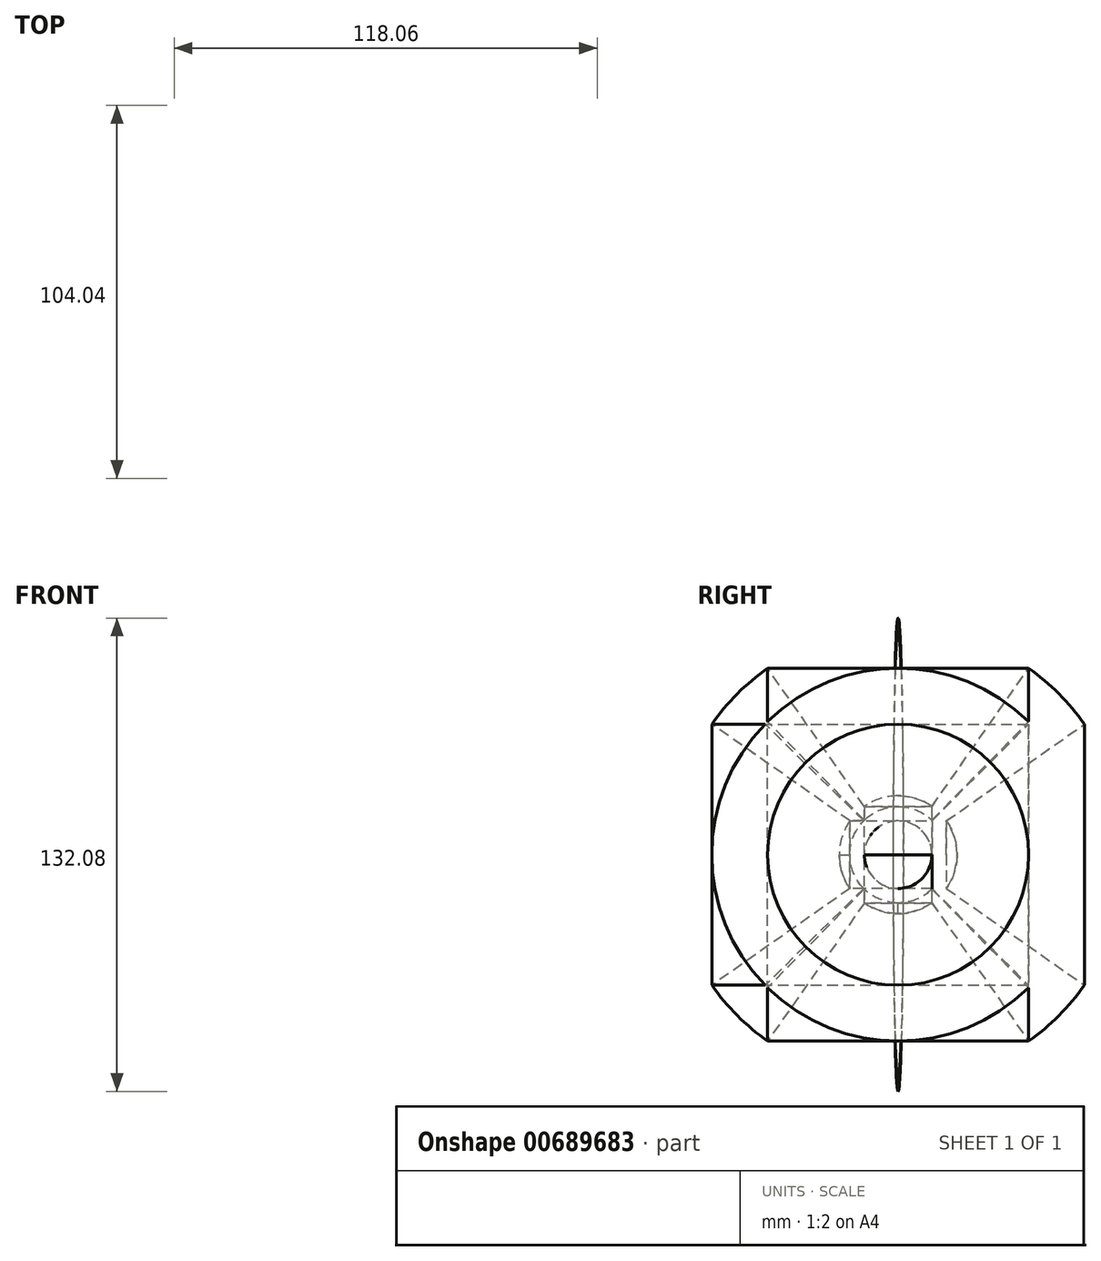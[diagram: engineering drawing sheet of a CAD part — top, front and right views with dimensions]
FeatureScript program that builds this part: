
annotation { "Feature Type Name" : "Feature", "Feature Type Description" : "" }
export const myFeature = defineFeature(function(context is Context, id is Id, definition is map)
    precondition{}
    {
        {
            var Q0;
            Q0=qCreatedBy(makeId("Front.planeOp"),FACE);
            var sketch = newSketch(context, id + "F0", { "sketchPlane" : qUnion([Q0])});
            skLineSegment(sketch, "E0", {"start": v(0, 0) * mm, "end": v(0, 63.5) * mm});
            skLineSegment(sketch, "E1", {"start": v(0, 0) * mm, "end": v(63.5, 0) * mm});
            skArc(sketch, "E2", {"start": v(63.5, 0) * mm, "mid": v(44.9, 44.9) * mm, "end": v(0, 63.5) * mm});
            skPoint(sketch, "E3", {"position": v(0, 16.43) * mm});
            skPoint(sketch, "E4", {"position": v(0, 31.75) * mm});
            skPoint(sketch, "E5", {"position": v(0, 44.9) * mm});
            skPoint(sketch, "E6", {"position": v(0, 55) * mm});
            skPoint(sketch, "E7", {"position": v(0, 61.33) * mm});
            skLineSegment(sketch, "E8", {"start": v(0, 16.43) * mm, "end": v(61.34, 16.43) * mm});
            skLineSegment(sketch, "E9", {"start": v(0, 31.75) * mm, "end": v(55, 31.75) * mm});
            skLineSegment(sketch, "E10", {"start": v(0, 44.9) * mm, "end": v(44.9, 44.9) * mm});
            skLineSegment(sketch, "E11", {"start": v(0, 55) * mm, "end": v(31.75, 55) * mm});
            skLineSegment(sketch, "E12", {"start": v(0, 61.33) * mm, "end": v(16.44, 61.33) * mm});
            skLineSegment(sketch, "E13", {"start": v(61.34, 16.43) * mm, "end": v(61.34, 0) * mm});
            skLineSegment(sketch, "E14", {"start": v(16.44, 61.33) * mm, "end": v(16.44, 0) * mm});
            skLineSegment(sketch, "E15", {"start": v(31.75, 55) * mm, "end": v(31.75, 0) * mm});
            skLineSegment(sketch, "E16", {"start": v(44.9, 44.9) * mm, "end": v(44.9, 0) * mm});
            skLineSegment(sketch, "E17", {"start": v(55, 31.75) * mm, "end": v(55, 0) * mm});
            skSolve(sketch);
        }
        {
            var Q0;
            {var subQ0=sQuery(id+"F0.wireOp",EDGE,"E1");var subQ1=sQuery(id+"F0.wireOp",EDGE,"E0");var subQ2=makeQuery(id+"F0.imprint","INTERSECT",VERTEX,{"derivedFrom":[subQ1,subQ0]});Q0=makeQuery(id+"F0.imprint","IMPRINT",FACE,{"disambiguationData":[TD([[makeQuery(id+"F0.imprint","IMPRINT",EDGE,{"disambiguationData":[TD([[subQ2,-1.0]])],"derivedFrom":subQ1}),-1.0]])]});}
            var Q1;
            {var subQ0=sQuery(id+"F0.wireOp",EDGE,"E15");var subQ1=sQuery(id+"F0.wireOp",EDGE,"E8");var subQ2=makeQuery(id+"F0.imprint","INTERSECT",VERTEX,{"derivedFrom":[subQ1,subQ0]});Q1=makeQuery(id+"F0.imprint","IMPRINT",FACE,{"disambiguationData":[TD([[makeQuery(id+"F0.imprint","IMPRINT",EDGE,{"disambiguationData":[TD([[subQ2,-1.0]])],"derivedFrom":subQ1}),1.0]])]});}
            var Q2;
            {var subQ0=sQuery(id+"F0.wireOp",EDGE,"E13");Q2=makeQuery(id+"F0.imprint","IMPRINT",FACE,{"disambiguationData":[TD([[makeQuery(id+"F0.imprint","IMPRINT",EDGE,{"derivedFrom":subQ0}),-1.0]])]});}
            var Q3;
            {var subQ3=sQuery(id+"F0.wireOp",EDGE,"E13");Q3=makeQuery(id+"F0.imprint","IMPRINT",FACE,{"disambiguationData":[TD([[makeQuery(id+"F0.imprint","IMPRINT",EDGE,{"derivedFrom":subQ3}),1.0]])]});}
            var Q4;
            {var subQ0=sQuery(id+"F0.wireOp",EDGE,"E14");var subQ1=sQuery(id+"F0.wireOp",EDGE,"E10");var subQ2=makeQuery(id+"F0.imprint","INTERSECT",VERTEX,{"derivedFrom":[subQ1,subQ0]});Q4=makeQuery(id+"F0.imprint","IMPRINT",FACE,{"disambiguationData":[TD([[makeQuery(id+"F0.imprint","IMPRINT",EDGE,{"disambiguationData":[TD([[subQ2,-1.0]])],"derivedFrom":subQ1}),1.0]])]});}
            var Q5;
            {var subQ3=sQuery(id+"F0.wireOp",EDGE,"E12");Q5=makeQuery(id+"F0.imprint","IMPRINT",FACE,{"disambiguationData":[TD([[makeQuery(id+"F0.imprint","IMPRINT",EDGE,{"derivedFrom":subQ3}),1.0]])]});}
            var Q6;
            {var subQ0=sQuery(id+"F0.wireOp",EDGE,"E16");var subQ1=sQuery(id+"F0.wireOp",EDGE,"E1");var subQ2=makeQuery(id+"F0.imprint","INTERSECT",VERTEX,{"derivedFrom":[subQ1,subQ0]});Q6=makeQuery(id+"F0.imprint","IMPRINT",FACE,{"disambiguationData":[TD([[makeQuery(id+"F0.imprint","IMPRINT",EDGE,{"disambiguationData":[TD([[subQ2,-1.0]])],"derivedFrom":subQ1}),1.0]])]});}
            var Q7;
            {var subQ0=sQuery(id+"F0.wireOp",EDGE,"E8");var subQ3=sQuery(id+"F0.wireOp",EDGE,"E17");var subQ5=makeQuery(id+"F0.imprint","INTERSECT",VERTEX,{"derivedFrom":[subQ0,subQ3]});Q7=makeQuery(id+"F0.imprint","IMPRINT",FACE,{"disambiguationData":[TD([[makeQuery(id+"F0.imprint","IMPRINT",EDGE,{"disambiguationData":[TD([[subQ5,-1.0]])],"derivedFrom":subQ0}),1.0]])]});}
            var Q8;
            {var subQ0=sQuery(id+"F0.wireOp",EDGE,"E9");var subQ3=sQuery(id+"F0.wireOp",EDGE,"E16");var subQ5=makeQuery(id+"F0.imprint","INTERSECT",VERTEX,{"derivedFrom":[subQ0,subQ3]});Q8=makeQuery(id+"F0.imprint","IMPRINT",FACE,{"disambiguationData":[TD([[makeQuery(id+"F0.imprint","IMPRINT",EDGE,{"disambiguationData":[TD([[subQ5,-1.0]])],"derivedFrom":subQ0}),1.0]])]});}
            var Q9;
            {var subQ0=sQuery(id+"F0.wireOp",EDGE,"E14");var subQ1=sQuery(id+"F0.wireOp",EDGE,"E9");var subQ2=makeQuery(id+"F0.imprint","INTERSECT",VERTEX,{"derivedFrom":[subQ1,subQ0]});Q9=makeQuery(id+"F0.imprint","IMPRINT",FACE,{"disambiguationData":[TD([[makeQuery(id+"F0.imprint","IMPRINT",EDGE,{"disambiguationData":[TD([[subQ2,-1.0]])],"derivedFrom":subQ1}),1.0]])]});}
            var Q10;
            {var subQ0=sQuery(id+"F0.wireOp",EDGE,"E14");var subQ1=sQuery(id+"F0.wireOp",EDGE,"E8");var subQ2=makeQuery(id+"F0.imprint","INTERSECT",VERTEX,{"derivedFrom":[subQ1,subQ0]});Q10=makeQuery(id+"F0.imprint","IMPRINT",FACE,{"disambiguationData":[TD([[makeQuery(id+"F0.imprint","IMPRINT",EDGE,{"disambiguationData":[TD([[subQ2,-1.0]])],"derivedFrom":subQ1}),1.0]])]});}
            var Q11;
            {var subQ0=sQuery(id+"F0.wireOp",EDGE,"E10");var subQ3=sQuery(id+"F0.wireOp",EDGE,"E15");var subQ5=makeQuery(id+"F0.imprint","INTERSECT",VERTEX,{"derivedFrom":[subQ0,subQ3]});Q11=makeQuery(id+"F0.imprint","IMPRINT",FACE,{"disambiguationData":[TD([[makeQuery(id+"F0.imprint","IMPRINT",EDGE,{"disambiguationData":[TD([[subQ5,-1.0]])],"derivedFrom":subQ0}),1.0]])]});}
            var Q12;
            {var subQ0=sQuery(id+"F0.wireOp",EDGE,"E11");var subQ3=sQuery(id+"F0.wireOp",EDGE,"E14");var subQ5=makeQuery(id+"F0.imprint","INTERSECT",VERTEX,{"derivedFrom":[subQ0,subQ3]});Q12=makeQuery(id+"F0.imprint","IMPRINT",FACE,{"disambiguationData":[TD([[makeQuery(id+"F0.imprint","IMPRINT",EDGE,{"disambiguationData":[TD([[subQ5,-1.0]])],"derivedFrom":subQ0}),1.0]])]});}
            var Q13;
            {var subQ0=sQuery(id+"F0.wireOp",EDGE,"E8");var subQ1=sQuery(id+"F0.wireOp",EDGE,"E0");var subQ2=makeQuery(id+"F0.imprint","INTERSECT",VERTEX,{"derivedFrom":[subQ1,subQ0]});Q13=makeQuery(id+"F0.imprint","IMPRINT",FACE,{"disambiguationData":[TD([[makeQuery(id+"F0.imprint","IMPRINT",EDGE,{"disambiguationData":[TD([[subQ2,-1.0]])],"derivedFrom":subQ1}),-1.0]])]});}
            var Q14;
            {var subQ0=sQuery(id+"F0.wireOp",EDGE,"E9");var subQ1=sQuery(id+"F0.wireOp",EDGE,"E0");var subQ2=makeQuery(id+"F0.imprint","INTERSECT",VERTEX,{"derivedFrom":[subQ1,subQ0]});Q14=makeQuery(id+"F0.imprint","IMPRINT",FACE,{"disambiguationData":[TD([[makeQuery(id+"F0.imprint","IMPRINT",EDGE,{"disambiguationData":[TD([[subQ2,-1.0]])],"derivedFrom":subQ1}),-1.0]])]});}
            var Q15;
            {var subQ0=sQuery(id+"F0.wireOp",EDGE,"E10");var subQ1=sQuery(id+"F0.wireOp",EDGE,"E0");var subQ2=makeQuery(id+"F0.imprint","INTERSECT",VERTEX,{"derivedFrom":[subQ1,subQ0]});Q15=makeQuery(id+"F0.imprint","IMPRINT",FACE,{"disambiguationData":[TD([[makeQuery(id+"F0.imprint","IMPRINT",EDGE,{"disambiguationData":[TD([[subQ2,-1.0]])],"derivedFrom":subQ1}),-1.0]])]});}
            var Q16;
            {var subQ3=sQuery(id+"F0.wireOp",EDGE,"E12");Q16=makeQuery(id+"F0.imprint","IMPRINT",FACE,{"disambiguationData":[TD([[makeQuery(id+"F0.imprint","IMPRINT",EDGE,{"derivedFrom":subQ3}),-1.0]])]});}
            var Q17;
            {var subQ0=sQuery(id+"F0.wireOp",EDGE,"E16");var subQ1=sQuery(id+"F0.wireOp",EDGE,"E8");var subQ2=makeQuery(id+"F0.imprint","INTERSECT",VERTEX,{"derivedFrom":[subQ1,subQ0]});Q17=makeQuery(id+"F0.imprint","IMPRINT",FACE,{"disambiguationData":[TD([[makeQuery(id+"F0.imprint","IMPRINT",EDGE,{"disambiguationData":[TD([[subQ2,-1.0]])],"derivedFrom":subQ1}),1.0]])]});}
            var Q18;
            {var subQ0=sQuery(id+"F0.wireOp",EDGE,"E15");var subQ1=sQuery(id+"F0.wireOp",EDGE,"E9");var subQ2=makeQuery(id+"F0.imprint","INTERSECT",VERTEX,{"derivedFrom":[subQ1,subQ0]});Q18=makeQuery(id+"F0.imprint","IMPRINT",FACE,{"disambiguationData":[TD([[makeQuery(id+"F0.imprint","IMPRINT",EDGE,{"disambiguationData":[TD([[subQ2,-1.0]])],"derivedFrom":subQ1}),1.0]])]});}
            var Q19;
            {var subQ0=sQuery(id+"F0.wireOp",EDGE,"E14");var subQ1=sQuery(id+"F0.wireOp",EDGE,"E1");var subQ2=makeQuery(id+"F0.imprint","INTERSECT",VERTEX,{"derivedFrom":[subQ1,subQ0]});Q19=makeQuery(id+"F0.imprint","IMPRINT",FACE,{"disambiguationData":[TD([[makeQuery(id+"F0.imprint","IMPRINT",EDGE,{"disambiguationData":[TD([[subQ2,-1.0]])],"derivedFrom":subQ1}),1.0]])]});}
            var Q20;
            {var subQ0=sQuery(id+"F0.wireOp",EDGE,"E15");var subQ1=sQuery(id+"F0.wireOp",EDGE,"E1");var subQ2=makeQuery(id+"F0.imprint","INTERSECT",VERTEX,{"derivedFrom":[subQ1,subQ0]});Q20=makeQuery(id+"F0.imprint","IMPRINT",FACE,{"disambiguationData":[TD([[makeQuery(id+"F0.imprint","IMPRINT",EDGE,{"disambiguationData":[TD([[subQ2,-1.0]])],"derivedFrom":subQ1}),1.0]])]});}
            var Q21;
            Q21=sQuery(id+"F0.wireOp",EDGE,"E14");
            var Q22;
            Q22=sQuery(id+"F0.wireOp",EDGE,"E15");
            var Q23;
            Q23=sQuery(id+"F0.wireOp",EDGE,"E16");
            var Q24;
            Q24=sQuery(id+"F0.wireOp",EDGE,"E17");
            var Q25;
            Q25=sQuery(id+"F0.wireOp",EDGE,"E13");
            var Q26;
            Q26=sQuery(id+"F0.wireOp",EDGE,"E0");
            revolve(context, id + "F1", {"bodyType" : ToolBodyType.SURFACE, "entities" : qUnion([Q0, Q1, Q2, Q3, Q4, Q5, Q6, Q7, Q8, Q9, Q10, Q11, Q12, Q13, Q14, Q15, Q16, Q17, Q18, Q19, Q20]), "surfaceEntities" : qUnion([Q21, Q22, Q23, Q24, Q25]), "axis" : qUnion([Q26]), "revolveType" : RevolveType.FULL});
        }
        {
            var Q0;
            Q0=sQuery(id+"F0.wireOp",EDGE,"E12");
            var Q1;
            Q1=sQuery(id+"F0.wireOp",EDGE,"E11");
            var Q2;
            Q2=sQuery(id+"F0.wireOp",EDGE,"E10");
            var Q3;
            Q3=sQuery(id+"F0.wireOp",EDGE,"E9");
            var Q4;
            Q4=sQuery(id+"F0.wireOp",EDGE,"E8");
            var Q5;
            Q5=sQuery(id+"F0.wireOp",EDGE,"E1");
            revolve(context, id + "F2", {"bodyType" : ToolBodyType.SURFACE, "surfaceEntities" : qUnion([Q0, Q1, Q2, Q3, Q4]), "axis" : qUnion([Q5]), "revolveType" : RevolveType.FULL});
        }
        {
            var Q0;
            Q0=qCreatedBy(makeId("Right.planeOp"),FACE);
            var sketch = newSketch(context, id + "F3", { "sketchPlane" : qUnion([Q0])});
            skLineSegment(sketch, "E18", {"start": v(0, 0) * mm, "end": v(-63.5, 0) * mm});
            skLineSegment(sketch, "E19", {"start": v(0, 0) * mm, "end": v(0, 63.5) * mm});
            skArc(sketch, "E20", {"start": v(0, 63.5) * mm, "mid": v(-44.9, 44.9) * mm, "end": v(-63.5, 0) * mm});
            skPoint(sketch, "E21", {"position": v(-16.43, 0) * mm});
            skPoint(sketch, "E22", {"position": v(-31.75, 0) * mm});
            skPoint(sketch, "E23", {"position": v(-44.9, 0) * mm});
            skPoint(sketch, "E24", {"position": v(-55, 0) * mm});
            skPoint(sketch, "E25", {"position": v(-61.33, 0) * mm});
            skLineSegment(sketch, "E26", {"start": v(-16.43, 0) * mm, "end": v(-16.43, 61.34) * mm});
            skLineSegment(sketch, "E27", {"start": v(-31.75, 0) * mm, "end": v(-31.75, 55) * mm});
            skLineSegment(sketch, "E28", {"start": v(-44.9, 0) * mm, "end": v(-44.9, 44.9) * mm});
            skLineSegment(sketch, "E29", {"start": v(-55, 0) * mm, "end": v(-55, 31.75) * mm});
            skLineSegment(sketch, "E30", {"start": v(-61.33, 0) * mm, "end": v(-61.33, 16.44) * mm});
            skLineSegment(sketch, "E31", {"start": v(-16.43, 61.34) * mm, "end": v(0, 61.34) * mm});
            skLineSegment(sketch, "E32", {"start": v(-61.33, 16.44) * mm, "end": v(0, 16.44) * mm});
            skLineSegment(sketch, "E33", {"start": v(-55, 31.75) * mm, "end": v(0, 31.75) * mm});
            skLineSegment(sketch, "E34", {"start": v(-44.9, 44.9) * mm, "end": v(0, 44.9) * mm});
            skLineSegment(sketch, "E35", {"start": v(-31.75, 55) * mm, "end": v(0, 55) * mm});
            skSolve(sketch);
        }
        {
            var Q0;
            Q0=sQuery(id+"F3.wireOp",EDGE,"E32");
            var Q1;
            Q1=sQuery(id+"F3.wireOp",EDGE,"E34");
            var Q2;
            Q2=sQuery(id+"F3.wireOp",EDGE,"E33");
            var Q3;
            Q3=sQuery(id+"F3.wireOp",EDGE,"E35");
            var Q4;
            Q4=sQuery(id+"F3.wireOp",EDGE,"E31");
            var Q5;
            Q5=sQuery(id+"F3.wireOp",EDGE,"E18");
            revolve(context, id + "F4", {"bodyType" : ToolBodyType.SURFACE, "surfaceEntities" : qUnion([Q0, Q1, Q2, Q3, Q4]), "axis" : qUnion([Q5]), "revolveType" : RevolveType.FULL});
        }
        {
            var Q0;
            Q0=makeQuery(id+"F1.opRevolve","SWEPT_BODY",BODY,{"disambiguationData":[OSD([sQuery(id+"F0.wireOp",EDGE,"E13")])]});
            var Q1;
            Q1=makeQuery(id+"F1.opRevolve","SWEPT_BODY",BODY,{"disambiguationData":[OSD([sQuery(id+"F0.wireOp",EDGE,"E14")])]});
            var Q2;
            Q2=makeQuery(id+"F1.opRevolve","SWEPT_BODY",BODY,{"disambiguationData":[OSD([sQuery(id+"F0.wireOp",EDGE,"E15")])]});
            var Q3;
            Q3=makeQuery(id+"F1.opRevolve","SWEPT_BODY",BODY,{"disambiguationData":[OSD([sQuery(id+"F0.wireOp",EDGE,"E16")])]});
            var Q4;
            Q4=makeQuery(id+"F1.opRevolve","SWEPT_BODY",BODY,{"disambiguationData":[OSD([sQuery(id+"F0.wireOp",EDGE,"E17")])]});
            var Q5;
            Q5=qCreatedBy(makeId("Top.planeOp"),FACE);
            mirror(context, id + "F5", {"entities" : qUnion([Q0, Q1, Q2, Q3, Q4]), "mirrorPlane" : qUnion([Q5])});
        }
        {
            var Q0;
            Q0=makeQuery(id+"F2.opRevolve","SWEPT_BODY",BODY,{"disambiguationData":[OSD([sQuery(id+"F0.wireOp",EDGE,"E8")])]});
            var Q1;
            Q1=makeQuery(id+"F2.opRevolve","SWEPT_BODY",BODY,{"disambiguationData":[OSD([sQuery(id+"F0.wireOp",EDGE,"E9")])]});
            var Q2;
            Q2=makeQuery(id+"F2.opRevolve","SWEPT_BODY",BODY,{"disambiguationData":[OSD([sQuery(id+"F0.wireOp",EDGE,"E10")])]});
            var Q3;
            Q3=makeQuery(id+"F2.opRevolve","SWEPT_BODY",BODY,{"disambiguationData":[OSD([sQuery(id+"F0.wireOp",EDGE,"E11")])]});
            var Q4;
            Q4=makeQuery(id+"F2.opRevolve","SWEPT_BODY",BODY,{"disambiguationData":[OSD([sQuery(id+"F0.wireOp",EDGE,"E12")])]});
            var Q5;
            Q5=qCreatedBy(makeId("Right.planeOp"),FACE);
            mirror(context, id + "F6", {"entities" : qUnion([Q0, Q1, Q2, Q3, Q4]), "mirrorPlane" : qUnion([Q5])});
        }
        {
            var Q0;
            Q0=makeQuery(id+"F4.opRevolve","SWEPT_BODY",BODY,{"disambiguationData":[OSD([sQuery(id+"F3.wireOp",EDGE,"E31")])]});
            var Q1;
            Q1=makeQuery(id+"F4.opRevolve","SWEPT_BODY",BODY,{"disambiguationData":[OSD([sQuery(id+"F3.wireOp",EDGE,"E32")])]});
            var Q2;
            Q2=makeQuery(id+"F4.opRevolve","SWEPT_BODY",BODY,{"disambiguationData":[OSD([sQuery(id+"F3.wireOp",EDGE,"E33")])]});
            var Q3;
            Q3=makeQuery(id+"F4.opRevolve","SWEPT_BODY",BODY,{"disambiguationData":[OSD([sQuery(id+"F3.wireOp",EDGE,"E35")])]});
            var Q4;
            Q4=makeQuery(id+"F4.opRevolve","SWEPT_BODY",BODY,{"disambiguationData":[OSD([sQuery(id+"F3.wireOp",EDGE,"E34")])]});
            var Q5;
            Q5=qCreatedBy(makeId("Front.planeOp"),FACE);
            mirror(context, id + "F7", {"entities" : qUnion([Q0, Q1, Q2, Q3, Q4]), "mirrorPlane" : qUnion([Q5])});
        }
        {
            var Q0;
            Q0=qCreatedBy(makeId("Front.planeOp"),FACE);
            var sketch = newSketch(context, id + "F8", { "sketchPlane" : qUnion([Q0])});
            skLineSegment(sketch, "E36", {"start": v(0, 0) * mm, "end": v(16.44, 0) * mm});
            skLineSegment(sketch, "E37", {"start": v(0, 0) * mm, "end": v(0, 16.43) * mm});
            skLineSegment(sketch, "E38", {"start": v(13.46, 9.43) * mm, "end": v(52.02, 36.42) * mm});
            skLineSegment(sketch, "E39", {"start": v(9.43, 13.46) * mm, "end": v(36.42, 52.02) * mm});
            skPoint(sketch, "E40", {"position": v(16.44, 0) * mm});
            skPoint(sketch, "E41", {"position": v(0, 16.43) * mm});
            skArc(sketch, "E42", {"start": v(16.44, 0) * mm, "mid": v(15.68, 4.94) * mm, "end": v(13.46, 9.43) * mm});
            skArc(sketch, "E43.trimOffspring", {"start": v(9.43, 13.46) * mm, "mid": v(4.94, 15.67) * mm, "end": v(0, 16.43) * mm});
            skArc(sketch, "E44.trimOffspring", {"start": v(52.02, 36.42) * mm, "mid": v(44.9, 44.9) * mm, "end": v(36.42, 52.02) * mm});
            skSolve(sketch);
        }
        {
            var Q0;
            Q0=makeQuery(id+"F8.imprint","IMPRINT",FACE,{"disambiguationData":[TD([[makeQuery(id+"F8.imprint","IMPRINT",EDGE,{"derivedFrom":sQuery(id+"F8.wireOp",EDGE,"E36")}),1.0]])]});
            var Q1;
            Q1=makeQuery(id+"F1.opRevolve","SWEPT_EDGE",EDGE,{"disambiguationData":[OSD([sQuery(id+"F0.wireOp",VERTEX,"E16.start")])]});
            revolve(context, id + "F9", {"entities" : qUnion([Q0]), "axis" : qUnion([Q1]), "revolveType" : RevolveType.FULL});
        }
        {
            var Q0;
            Q0=makeQuery(id+"F8.imprint","IMPRINT",FACE,{"disambiguationData":[TD([[makeQuery(id+"F8.imprint","IMPRINT",EDGE,{"derivedFrom":sQuery(id+"F8.wireOp",EDGE,"E36")}),1.0]])]});
            var Q1;
            Q1=sQuery(id+"F8.wireOp",EDGE,"E36");
            revolve(context, id + "F10", {"operationType" : NewBodyOperationType.ADD, "entities" : qUnion([Q0]), "axis" : qUnion([Q1]), "revolveType" : RevolveType.FULL});
        }
        {
            var Q0;
            Q0=makeQuery(id+"F9.opRevolve","SWEPT_BODY",BODY,{"disambiguationData":[OSD([sQuery(id+"F8.wireOp",EDGE,"E36"),sQuery(id+"F8.wireOp",EDGE,"E37"),sQuery(id+"F8.wireOp",EDGE,"E38"),sQuery(id+"F8.wireOp",EDGE,"E39"),sQuery(id+"F8.wireOp",EDGE,"E42"),sQuery(id+"F8.wireOp",EDGE,"E43.trimOffspring"),sQuery(id+"F8.wireOp",EDGE,"E44.trimOffspring")])]});
            var Q1;
            Q1=qCreatedBy(makeId("Top.planeOp"),FACE);
            mirror(context, id + "F11", {"operationType" : NewBodyOperationType.ADD, "entities" : qUnion([Q0]), "mirrorPlane" : qUnion([Q1])});
        }
        {
            var Q0;
            Q0=makeQuery(id+"F9.opRevolve","SWEPT_BODY",BODY,{"disambiguationData":[OSD([sQuery(id+"F8.wireOp",EDGE,"E36"),sQuery(id+"F8.wireOp",EDGE,"E37"),sQuery(id+"F8.wireOp",EDGE,"E38"),sQuery(id+"F8.wireOp",EDGE,"E39"),sQuery(id+"F8.wireOp",EDGE,"E42"),sQuery(id+"F8.wireOp",EDGE,"E43.trimOffspring"),sQuery(id+"F8.wireOp",EDGE,"E44.trimOffspring")])]});
            var Q1;
            Q1=sQuery(id+"F8.wireOp",EDGE,"E36");
            transform(context, id + "F12", {"entities" : qUnion([Q0]), "transformType" : TransformType.ROTATION, "transformAxis" : qUnion([Q1]), "angle" : 90 * degree, "makeCopy" : true});
        }
        {
            var Q0;
            Q0=makeQuery(id+"F9.opRevolve","SWEPT_BODY",BODY,{"disambiguationData":[OSD([sQuery(id+"F8.wireOp",EDGE,"E36"),sQuery(id+"F8.wireOp",EDGE,"E37"),sQuery(id+"F8.wireOp",EDGE,"E38"),sQuery(id+"F8.wireOp",EDGE,"E39"),sQuery(id+"F8.wireOp",EDGE,"E42"),sQuery(id+"F8.wireOp",EDGE,"E43.trimOffspring"),sQuery(id+"F8.wireOp",EDGE,"E44.trimOffspring")])]});
            var Q1;
            Q1=sQuery(id+"F8.wireOp",EDGE,"E37");
            transform(context, id + "F13", {"entities" : qUnion([Q0]), "transformType" : TransformType.ROTATION, "transformAxis" : qUnion([Q1]), "angle" : 90 * degree, "makeCopy" : true});
        }
        {
            var Q0;
            Q0=qCreatedBy(makeId("Front.planeOp"),FACE);
            var sketch = newSketch(context, id + "F14", { "sketchPlane" : qUnion([Q0])});
            skArc(sketch, "E45", {"start": v(0, 63.5) * mm, "mid": v(-44.9, 44.9) * mm, "end": v(-63.5, 0) * mm});
            skPoint(sketch, "E46", {"position": v(-44.9, 44.9) * mm});
            skLineSegment(sketch, "E47", {"start": v(0, 63.5) * mm, "end": v(0, 66.04) * mm});
            skLineSegment(sketch, "E48", {"start": v(-63.5, 0) * mm, "end": v(-66.04, 0) * mm});
            skLineSegment(sketch, "E49", {"start": v(-44.9, 44.9) * mm, "end": v(-46.7, 46.7) * mm});
            skArc(sketch, "E50", {"start": v(0, 66.04) * mm, "mid": v(-46.7, 46.7) * mm, "end": v(-66.04, 0) * mm});
            skSolve(sketch);
        }
        {
            var Q0;
            {var subQ0=sQuery(id+"F14.wireOp",EDGE,"E48");Q0=makeQuery(id+"F14.imprint","IMPRINT",FACE,{"disambiguationData":[TD([[makeQuery(id+"F14.imprint","IMPRINT",EDGE,{"derivedFrom":subQ0}),-1.0]])]});}
            var Q1;
            {var subQ0=sQuery(id+"F14.wireOp",EDGE,"E47");Q1=makeQuery(id+"F14.imprint","IMPRINT",FACE,{"disambiguationData":[TD([[makeQuery(id+"F14.imprint","IMPRINT",EDGE,{"derivedFrom":subQ0}),1.0]])]});}
            var Q2;
            Q2=sQuery(id+"F14.wireOp",EDGE,"E45");
            var Q3;
            Q3=makeQuery(id+"F13.opPattern","COPY",EDGE,{"derivedFrom":makeQuery(id+"F9.opRevolve","SWEPT_EDGE",EDGE,{"disambiguationData":[OSD([sQuery(id+"F8.wireOp",EDGE,"E39"),sQuery(id+"F8.wireOp",EDGE,"E44.trimOffspring")])]}),"instanceName":"1"});
            revolve(context, id + "F15", {"entities" : qUnion([Q0, Q1]), "surfaceEntities" : qUnion([Q2]), "axis" : qUnion([Q3]), "revolveType" : RevolveType.SYMMETRIC, "angle" : 2.5 * degree});
        }
        {
            var Q0;
            Q0=makeQuery(id+"F15.opRevolve","SWEPT_BODY",BODY,{"disambiguationData":[OSD([sQuery(id+"F14.wireOp",EDGE,"E45"),sQuery(id+"F14.wireOp",EDGE,"E47"),sQuery(id+"F14.wireOp",EDGE,"E48"),sQuery(id+"F14.wireOp",EDGE,"E50")])]});
            var Q1;
            Q1=qCreatedBy(makeId("Top.planeOp"),FACE);
            mirror(context, id + "F16", {"operationType" : NewBodyOperationType.ADD, "entities" : qUnion([Q0]), "mirrorPlane" : qUnion([Q1])});
        }
    });
